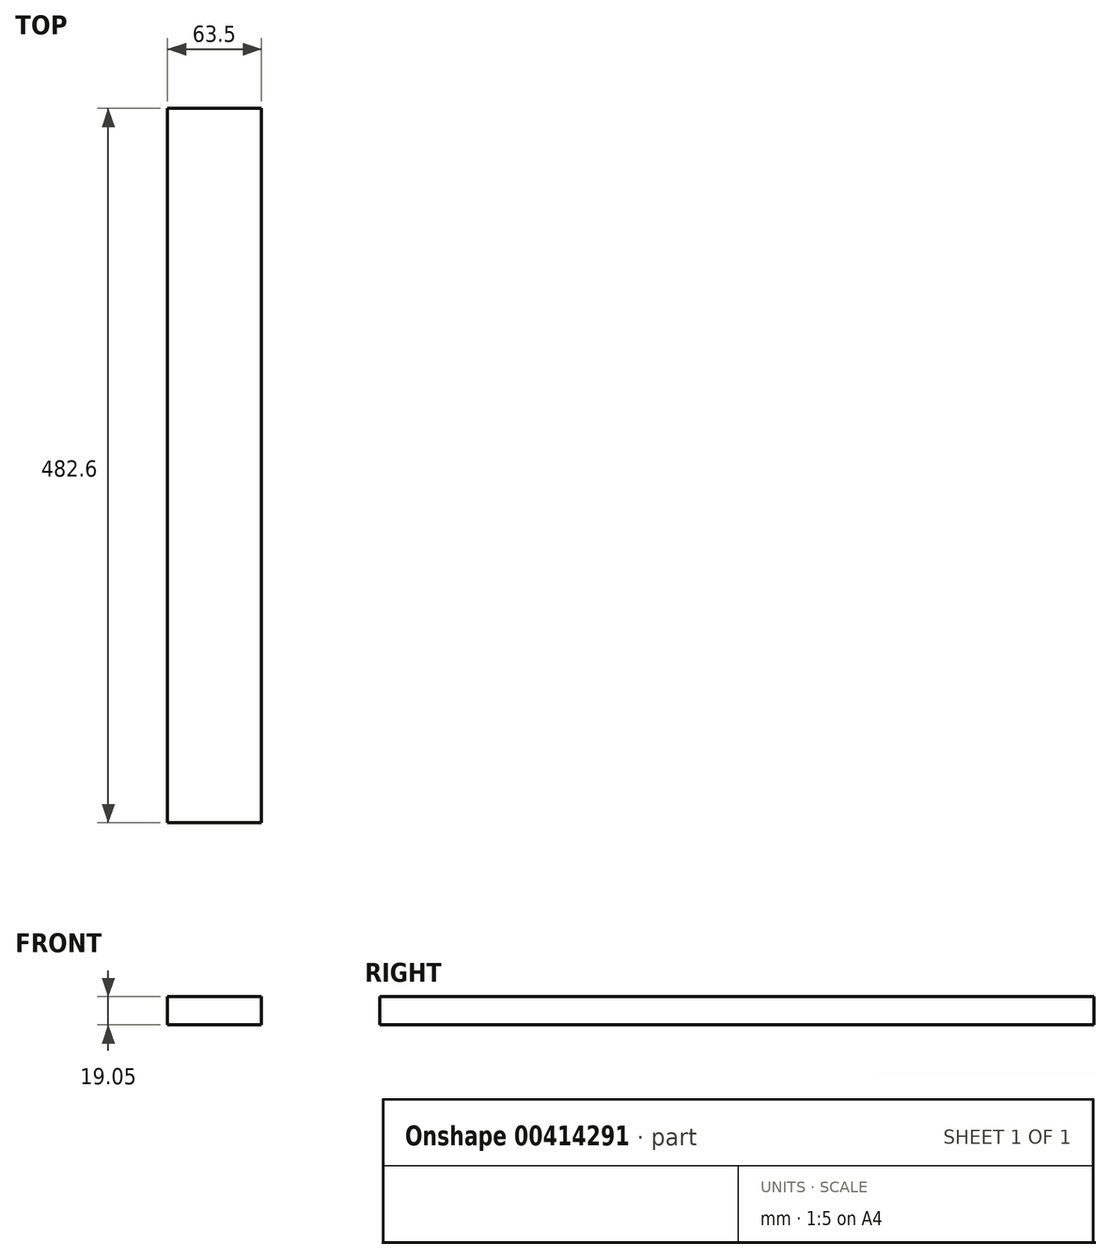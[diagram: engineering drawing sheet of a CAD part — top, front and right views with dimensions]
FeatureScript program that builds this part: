
annotation { "Feature Type Name" : "Feature", "Feature Type Description" : "" }
export const myFeature = defineFeature(function(context is Context, id is Id, definition is map)
    precondition{}
    {
        {
            var Q0;
            Q0=qCreatedBy(makeId("Front.planeOp"),FACE);
            var sketch = newSketch(context, id + "F0", { "sketchPlane" : qUnion([Q0])});
            skLineSegment(sketch, "E0.bottom", {"start": v(0, 0) * mm, "end": v(-63.5, 0) * mm});
            skLineSegment(sketch, "E0.top", {"start": v(0, 19.05) * mm, "end": v(-63.5, 19.05) * mm});
            skLineSegment(sketch, "E0.left", {"start": v(0, 0) * mm, "end": v(0, 19.05) * mm});
            skLineSegment(sketch, "E0.right", {"start": v(-63.5, 0) * mm, "end": v(-63.5, 19.05) * mm});
            skSolve(sketch);
        }
        {
            var Q0;
            Q0=qSketchRegion(id+"F0",true);
            extrude(context, id + "F1", {"entities" : qUnion([Q0]), "depth" : 482.6 * mm});
        }
    });
